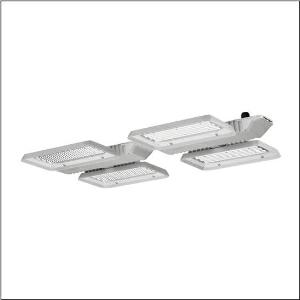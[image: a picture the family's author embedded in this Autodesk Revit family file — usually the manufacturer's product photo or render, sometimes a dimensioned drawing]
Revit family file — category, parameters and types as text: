
# Revit family: highbay_11_51hla2d24mca
name_source: partatom
category: Lighting Fixtures
units: mm (PartAtom-declared; Revit-internal decimal feet)

## family parameters
Cut with Voids When Loaded = No
Host = Face
Light Source = No
Part Type = Normal
Room Calculation Point = No
Round Connector Dimension = Use Diameter
Shared = No

## types (1)
- --- (1 x LED, 28800 lm, 162.4 W, 4000K)
    Apparent Load = 162 VA
    CIE Flux Codes = 89 96 99 100 100
    Color Rendering = 80
    Color Temperature = 4000K
    Default Elevation = 1800 mm
    Description = Highbay 11, LED high bay luminaire, primary light control with lens, of PMMA, light emission: direct distribution, primary light characteristic: symmetric, installation type: surface-mounted, suspended mounting, for 2x 2x LED, rated luminous flux: 28.800lm, luminous efficacy: 177lm/W, light colour: 840, colour temperature: 4000K, control gear: ECG DALI, with terminal, 5-pole, max. 2.5mm², mains connection: 230..240V, AC, 50/60Hz, rated input power: 162W, LED unit, of diecast aluminium, unplated, bead blasted, silver, length: 940mm, width: 500mm, height: 65mm, housing, of diecast aluminium, uncoated, bead blasted, silver, protection rating (complete): IP65, insulation class (complete): insulation class I (protective earthing), certification: CE, ENEC, VDE, UKCA, protection symbol: D, impact resistance: IK08 with glass or PC cover, permissible operating ambient temperature: -35..+55°C, reducing of maximum allowable ambient temperature of 5°C with ceiling mounting, corresponds to IFS (International Featured Standards) requirements for safety and quality in the food industry, packaging unit: 1 piece
    Height = 95 mm
    Lamp = 1 x LED
    Lamp Light Flux = 28800 lm
    Lamp Power = 162.4 W
    Lamp count = 1
    Length = 939 mm
    Luminous efficacy = 177 lm/W
    Manufacturer = Siteco
    ModVariant = No
    Model = 51HLA2D24MCA
    Mounting Place = Ceiling
    Mounting Type = Pendant
    Number of Poles = 1
    OnlyDefault = Yes
    Power Factor = 1
    Product Name = Highbay 11
    Product group = LED high bay luminaire
    ProductGroupID = 903
    Protection Class = Protection class I
    Protection Degree = IP 65
    RLX_Detail_Level = 1
    RLX_Emergency_Light_Flux = 0 lm
    RLX_Emergency_Type = 0
    RLX_Emergency_Type_DB = No
    RlxData = <blob elided: 96665 chars, md5=499d5f37>
    Socket = socket
    Standby Power = 0 W
    System Light Flux = 28800 lm
    System Power = 162 W
    Type Comments = factory setting: luminous flux: 100 % | dim-lin: 254 | 460 mA
    Type Image = l_1003428.jpg
    URL = http://relux.com
    VarID = @adj_145965
    Voltage = 0 V
    Weight = 0.00 kg
    Width = 501 mm

## geometry (parser evidence)
native form markers: Blend x4, Sweep x11
no freeform markers — native parametric forms only
